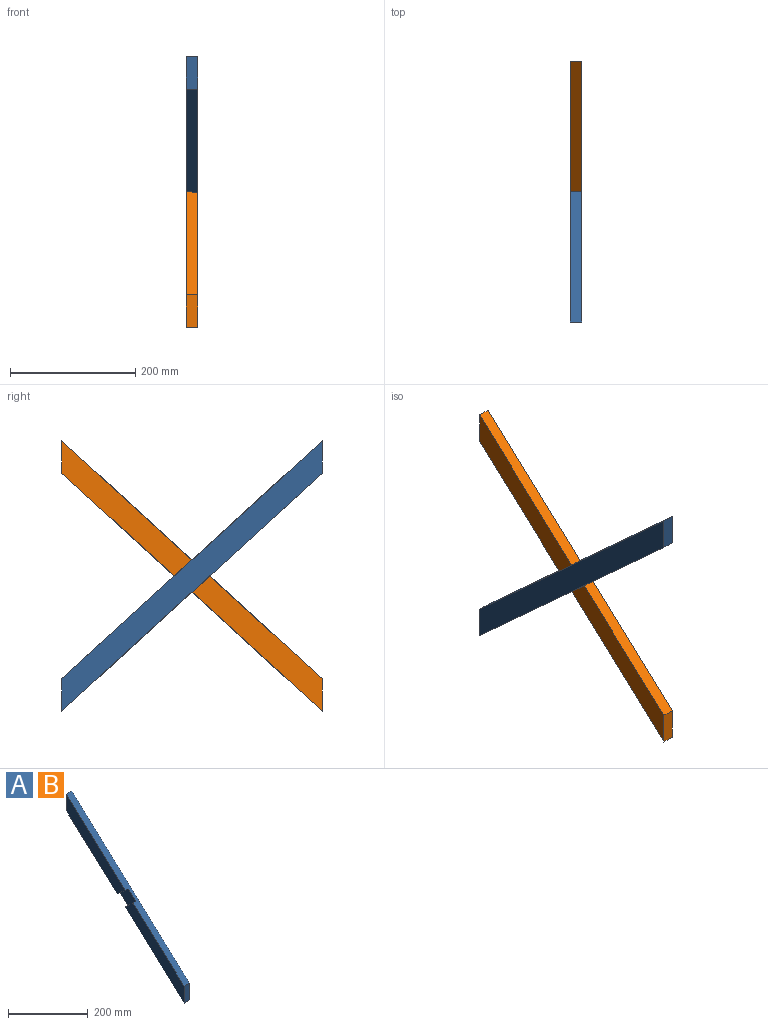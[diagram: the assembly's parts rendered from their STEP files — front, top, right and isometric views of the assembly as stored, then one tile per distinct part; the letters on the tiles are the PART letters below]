
ASSEMBLY  parts=2 mates=1
PART A: 10 faces, bbox 19.1x415.9x431.8 mm
  f0: plane 415.93x380.18mm, normal (0,0.67,-0.74), area 10370.3mm2, adj f1,f3,f4,f5,f6,f7,f8,f9
  f1: plane 51.62x19.05mm, normal (0,1,0), area 983.3mm2, adj f0,f2,f5,f9
  f2: plane 415.93x380.18mm, normal (0,-0.67,0.74), area 10370.3mm2, adj f1,f3,f4,f5,f6,f7,f8,f9
  f3: plane 51.62x19.05mm, normal (0,-1,0), area 983.3mm2, adj f0,f2,f5,f7
  f4: plane 56.47x51.62mm, normal (-1,0,0), area 1457.5mm2, adj f0,f2,f6,f8
  f5: plane 431.8x415.93mm, normal (1,0,0), area 21469.3mm2, adj f0,f1,f2,f3
  f6: plane 28.24x25.81mm, normal (0,0.67,0.74), area 364.4mm2, adj f0,f2,f4,f7
  f7: plane 215.9x207.96mm, normal (-1,0,0), area 10005.9mm2, adj f0,f2,f3,f6
  f8: plane 28.24x25.81mm, normal (0,-0.67,-0.74), area 364.4mm2, adj f0,f2,f4,f9
  f9: plane 215.9x207.96mm, normal (-1,0,0), area 10005.9mm2, adj f0,f1,f2,f8
PART B: same geometry as A
PLACE A rot(axis=(0,0,-1),180deg) t=(1495.2,556.95,-250.39)mm
PLACE B t=(-822.55,39.42,-250.39)mm
MATE fastened A.f4 <-> B.f4  axis (1,0,0) through (336.33,298.19,181.82)mm
